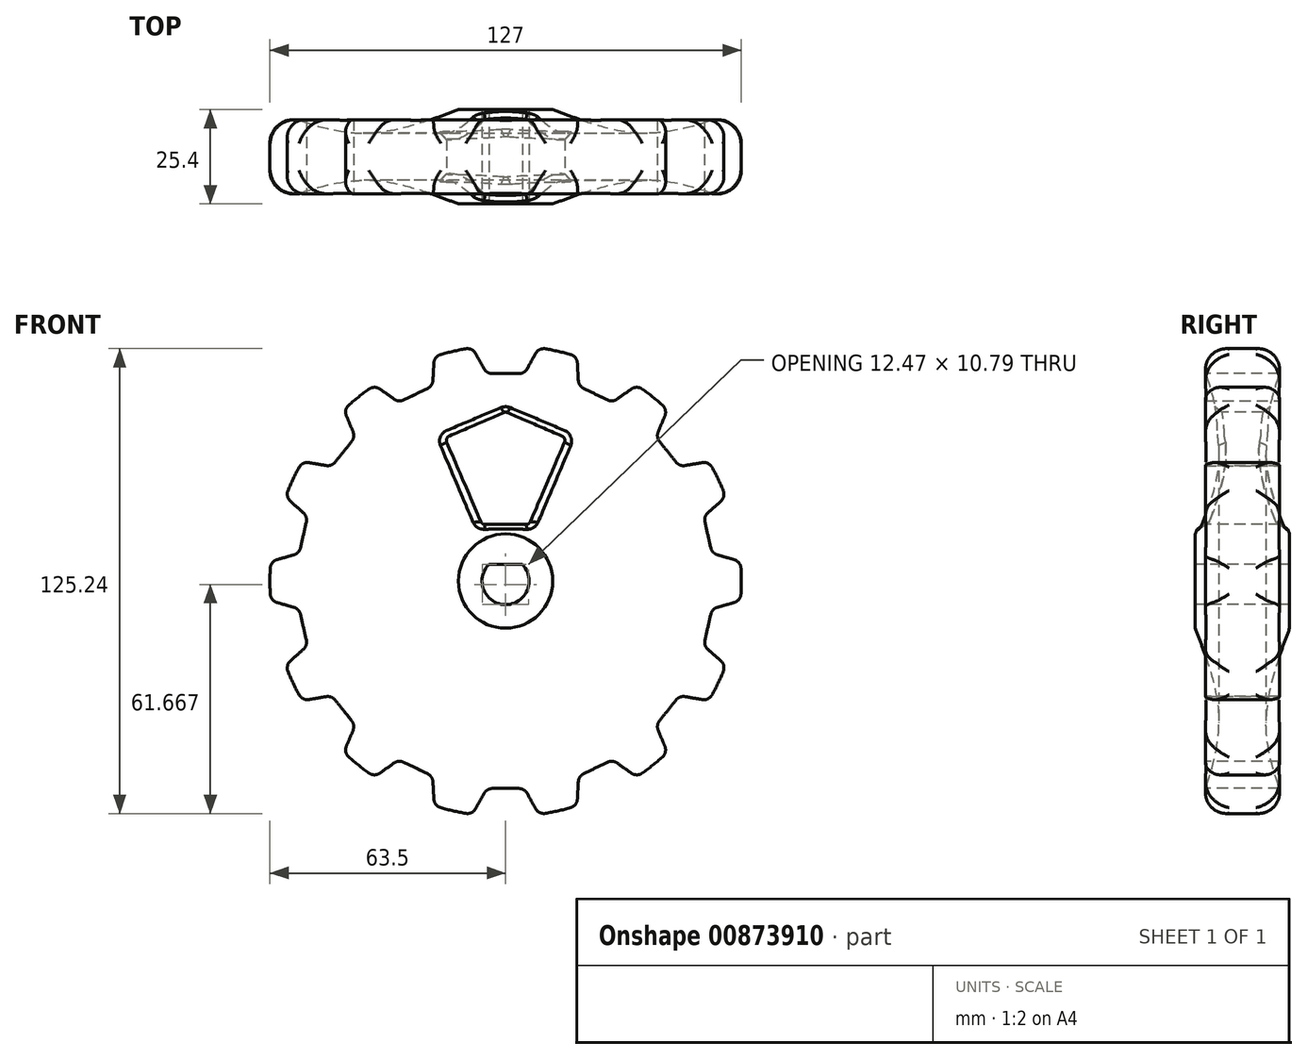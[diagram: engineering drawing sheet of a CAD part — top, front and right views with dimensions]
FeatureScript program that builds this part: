
annotation { "Feature Type Name" : "Feature", "Feature Type Description" : "" }
export const myFeature = defineFeature(function(context is Context, id is Id, definition is map)
    precondition{}
    {
        {
            var Q0;
            Q0=qCreatedBy(makeId("Right.planeOp"),FACE);
            var sketch = newSketch(context, id + "F0", { "sketchPlane" : qUnion([Q0])});
            skLineSegment(sketch, "E0", {"start": v(0, 0) * mm, "end": v(12.7, 0) * mm});
            skLineSegment(sketch, "E1", {"start": v(12.7, 0) * mm, "end": v(12.7, 12.7) * mm});
            skFitSpline(sketch, "E2", {"points": [v(12.7, 63.5) * mm, v(6.35, 38.1) * mm, v(12.7, 12.7) * mm], "startDerivative": vector(-19.05, -50.8) * mm, "endDerivative": vector(19.05, -50.8) * mm});
            skLineSegment(sketch, "E3", {"start": v(3.65, 63.5) * mm, "end": v(-3.65, 63.5) * mm});
            skFitSpline(sketch, "E4.MirrorCS", {"points": [v(-12.7, 63.5) * mm, v(-6.35, 38.1) * mm, v(-12.7, 12.7) * mm], "startDerivative": vector(19.05, -50.8) * mm, "endDerivative": vector(-19.05, -50.8) * mm});
            skLineSegment(sketch, "E5.MirrorCS", {"start": v(-12.7, 0) * mm, "end": v(-12.7, 12.7) * mm});
            skLineSegment(sketch, "E6.MirrorCS", {"start": v(0, 0) * mm, "end": v(-12.7, 0) * mm});
            skArc(sketch, "E7.filletArc", {"start": v(9.68, 55.14) * mm, "mid": v(8.8, 60.86) * mm, "end": v(3.65, 63.5) * mm});
            skArc(sketch, "E8.filletArc", {"start": v(-3.65, 63.5) * mm, "mid": v(-8.8, 60.86) * mm, "end": v(-9.68, 55.14) * mm});
            skSolve(sketch);
        }
        {
            var Q0;
            Q0=makeQuery(id+"F0.imprint","IMPRINT",FACE,{"disambiguationData":[TD([[makeQuery(id+"F0.imprint","IMPRINT",EDGE,{"derivedFrom":sQuery(id+"F0.wireOp",EDGE,"E0")}),1.0]])]});
            var Q1;
            Q1=sQuery(id+"F0.wireOp",EDGE,"E6.MirrorCS");
            revolve(context, id + "F1", {"surfaceOperationType" : NewSurfaceOperationType.NEW, "entities" : qUnion([Q0]), "axis" : qUnion([Q1]), "revolveType" : RevolveType.FULL});
        }
        {
            var Q0;
            Q0=qCreatedBy(makeId("Front.planeOp"),FACE);
            var sketch = newSketch(context, id + "F2", { "sketchPlane" : qUnion([Q0])});
            skLineSegment(sketch, "E9", {"start": v(0, 0) * mm, "end": v(0, 55.88) * mm});
            skLineSegment(sketch, "E10", {"start": v(0, 55.88) * mm, "end": v(-5.08, 55.88) * mm});
            skLineSegment(sketch, "E11", {"start": v(0, 55.88) * mm, "end": v(0, 66.04) * mm});
            skLineSegment(sketch, "E12", {"start": v(0, 66.04) * mm, "end": v(-10.67, 66.04) * mm});
            skLineSegment(sketch, "E13", {"start": v(-10.67, 66.04) * mm, "end": v(-5.08, 55.88) * mm});
            skLineSegment(sketch, "E14.MirrorCS", {"start": v(10.67, 66.04) * mm, "end": v(5.08, 55.88) * mm});
            skLineSegment(sketch, "E15.MirrorCS", {"start": v(0, 55.88) * mm, "end": v(5.08, 55.88) * mm});
            skLineSegment(sketch, "E16.MirrorCS", {"start": v(0, 66.04) * mm, "end": v(10.67, 66.04) * mm});
            skSolve(sketch);
        }
        {
            var Q0;
            Q0=makeQuery(id+"F2.imprint","IMPRINT",FACE,{"disambiguationData":[TD([[makeQuery(id+"F2.imprint","IMPRINT",EDGE,{"derivedFrom":sQuery(id+"F2.wireOp",EDGE,"E11")}),-1.0]])]});
            var Q1;
            Q1=makeQuery(id+"F2.imprint","IMPRINT",FACE,{"disambiguationData":[TD([[makeQuery(id+"F2.imprint","IMPRINT",EDGE,{"derivedFrom":sQuery(id+"F2.wireOp",EDGE,"E10")}),-1.0]])]});
            extrude(context, id + "F3", {"entities" : qUnion([Q0, Q1]), "operationType" : NewBodyOperationType.REMOVE, "oppositeDirection" : true, "depth" : 25.4 * mm, "offsetDistance" : 25.4 * mm, "symmetric" : true});
        }
        {
            var Q0;
            Q0=makeQuery(id+"F3.boolean.opBoolean","COPY",EDGE,{"derivedFrom":makeQuery(id+"F3.opExtrude","SWEPT_EDGE",EDGE,{"disambiguationData":[OSD([sQuery(id+"F2.wireOp",EDGE,"E10"),sQuery(id+"F2.wireOp",EDGE,"E13")])]})});
            var Q1;
            Q1=makeQuery(id+"F3.boolean.opBoolean","COPY",EDGE,{"derivedFrom":makeQuery(id+"F3.opExtrude","SWEPT_EDGE",EDGE,{"disambiguationData":[OSD([sQuery(id+"F2.wireOp",EDGE,"E14.MirrorCS"),sQuery(id+"F2.wireOp",EDGE,"E15.MirrorCS")])]})});
            fillet(context, id + "F4", {"entities" : qUnion([Q0, Q1]), "radius" : 2.54 * mm, "tangentPropagation" : true, "allowEdgeOverflow" : false});
        }
        {
            var Q0;
            Q0=makeQuery(id+"F3.boolean.opBoolean","INTERSECT",EDGE,{"derivedFrom":[makeQuery(id+"F1.opRevolve","SWEPT_FACE",FACE,{"disambiguationData":[OSD([sQuery(id+"F0.wireOp",EDGE,"E3")])]}),makeQuery(id+"F3.opExtrude","SWEPT_FACE",FACE,{"disambiguationData":[OSD([sQuery(id+"F2.wireOp",EDGE,"E13")])]})]});
            var Q1;
            Q1=makeQuery(id+"F3.boolean.opBoolean","INTERSECT",EDGE,{"derivedFrom":[makeQuery(id+"F1.opRevolve","SWEPT_FACE",FACE,{"disambiguationData":[OSD([sQuery(id+"F0.wireOp",EDGE,"E3")])]}),makeQuery(id+"F3.opExtrude","SWEPT_FACE",FACE,{"disambiguationData":[OSD([sQuery(id+"F2.wireOp",EDGE,"E14.MirrorCS")])]})]});
            fillet(context, id + "F5", {"entities" : qUnion([Q0, Q1]), "radius" : 2.54 * mm, "allowEdgeOverflow" : false});
        }
        {
            var Q0;
            Q0=makeQuery(id+"F5.opFillet","BLEND_FACE",FACE,{"disambiguationData":[OSD([sQuery(id+"F0.wireOp",EDGE,"E3"),sQuery(id+"F2.wireOp",EDGE,"E14.MirrorCS")])]});
            var Q1;
            Q1=makeQuery(id+"F3.boolean.opBoolean","COPY",FACE,{"derivedFrom":makeQuery(id+"F3.opExtrude","SWEPT_FACE",FACE,{"disambiguationData":[OSD([sQuery(id+"F2.wireOp",EDGE,"E14.MirrorCS")])]})});
            var Q2;
            Q2=makeQuery(id+"F4.opFillet","BLEND_FACE",FACE,{"disambiguationData":[OSD([sQuery(id+"F2.wireOp",EDGE,"E14.MirrorCS"),sQuery(id+"F2.wireOp",EDGE,"E15.MirrorCS")])]});
            var Q3;
            Q3=makeQuery(id+"F3.boolean.opBoolean","COPY",FACE,{"derivedFrom":makeQuery(id+"F3.opExtrude","SWEPT_FACE",FACE,{"disambiguationData":[OSD([sQuery(id+"F2.wireOp",EDGE,"E10"),sQuery(id+"F2.wireOp",EDGE,"E15.MirrorCS")])]})});
            var Q4;
            Q4=makeQuery(id+"F4.opFillet","BLEND_FACE",FACE,{"disambiguationData":[OSD([sQuery(id+"F2.wireOp",EDGE,"E10"),sQuery(id+"F2.wireOp",EDGE,"E13")])]});
            var Q5;
            Q5=makeQuery(id+"F3.boolean.opBoolean","COPY",FACE,{"derivedFrom":makeQuery(id+"F3.opExtrude","SWEPT_FACE",FACE,{"disambiguationData":[OSD([sQuery(id+"F2.wireOp",EDGE,"E13")])]})});
            var Q6;
            Q6=makeQuery(id+"F5.opFillet","BLEND_FACE",FACE,{"disambiguationData":[OSD([sQuery(id+"F0.wireOp",EDGE,"E3"),sQuery(id+"F2.wireOp",EDGE,"E13")])]});
            var Q7;
            Q7=makeQuery(id+"F1.opRevolve","SWEPT_EDGE",EDGE,{"disambiguationData":[OSD([sQuery(id+"F0.wireOp",EDGE,"E4.MirrorCS"),sQuery(id+"F0.wireOp",EDGE,"E5.MirrorCS")])]});
            circularPattern(context, id + "F6", {"patternType" : PatternType.FACE, "faces" : qUnion([Q0, Q1, Q2, Q3, Q4, Q5, Q6]), "axis" : qUnion([Q7]), "angle" : 360 * degree, "instanceCount" : 14, "equalSpace" : true});
        }
        {
            var Q0;
            Q0=makeQuery(id+"F1.opRevolve","SWEPT_FACE",FACE,{"disambiguationData":[OSD([sQuery(id+"F0.wireOp",EDGE,"E5.MirrorCS")])]});
            var sketch = newSketch(context, id + "F7", { "sketchPlane" : qUnion([Q0])});
            skLineSegment(sketch, "E17", {"start": v(0, 0) * mm, "end": v(0, 15.24) * mm});
            skLineSegment(sketch, "E18", {"start": v(0, 15.24) * mm, "end": v(5.51, 15.24) * mm});
            skLineSegment(sketch, "E19", {"start": v(6.68, 16) * mm, "end": v(15.86, 37.42) * mm});
            skLineSegment(sketch, "E20", {"start": v(15.2, 39.08) * mm, "end": v(0.5, 45.39) * mm});
            skPoint(sketch, "E21.visualSharp", {"position": v(16.36, 38.58) * mm});
            skArc(sketch, "E21.filletArc", {"start": v(15.86, 37.42) * mm, "mid": v(15.87, 38.39) * mm, "end": v(15.2, 39.08) * mm});
            skPoint(sketch, "E22.visualSharp", {"position": v(6.35, 15.24) * mm});
            skArc(sketch, "E22.filletArc", {"start": v(5.51, 15.24) * mm, "mid": v(6.21, 15.45) * mm, "end": v(6.68, 16) * mm});
            skLineSegment(sketch, "E23.MirrorCS", {"start": v(-15.2, 39.08) * mm, "end": v(-0.5, 45.39) * mm});
            skArc(sketch, "E24.MirrorCS", {"start": v(-15.86, 37.42) * mm, "mid": v(-15.87, 38.39) * mm, "end": v(-15.2, 39.08) * mm});
            skLineSegment(sketch, "E25.MirrorCS", {"start": v(-6.68, 16) * mm, "end": v(-15.86, 37.42) * mm});
            skArc(sketch, "E26.MirrorCS", {"start": v(-5.51, 15.24) * mm, "mid": v(-6.21, 15.45) * mm, "end": v(-6.68, 16) * mm});
            skLineSegment(sketch, "E27.MirrorCS", {"start": v(0, 15.24) * mm, "end": v(-5.51, 15.24) * mm});
            skPoint(sketch, "E28.visualSharp", {"position": v(0, 45.6) * mm});
            skArc(sketch, "E28.filletArc", {"start": v(0.5, 45.39) * mm, "mid": v(0, 45.49) * mm, "end": v(-0.5, 45.39) * mm});
            skSolve(sketch);
        }
        {
            var Q0;
            Q0=makeQuery(id+"F7.imprint","IMPRINT",FACE,{"disambiguationData":[TD([[makeQuery(id+"F7.imprint","IMPRINT",EDGE,{"derivedFrom":sQuery(id+"F7.wireOp",EDGE,"E18")}),1.0]])]});
            extrude(context, id + "F8", {"entities" : qUnion([Q0]), "operationType" : NewBodyOperationType.REMOVE, "oppositeDirection" : true, "depth" : 25.4 * mm, "offsetDistance" : 25.4 * mm});
        }
        {
            var Q0;
            Q0=makeQuery(id+"F8.boolean.opBoolean","INTERSECT",EDGE,{"derivedFrom":[makeQuery(id+"F1.opRevolve","SWEPT_FACE",FACE,{"disambiguationData":[OSD([sQuery(id+"F0.wireOp",EDGE,"E4.MirrorCS")])]}),makeQuery(id+"F8.opExtrude","SWEPT_FACE",FACE,{"disambiguationData":[OSD([sQuery(id+"F7.wireOp",EDGE,"E23.MirrorCS")])]})]});
            var Q1;
            Q1=makeQuery(id+"FnRsK331Qt2ESd3_1.4.F8.boolean.opBoolean","INTERSECT",EDGE,{"derivedFrom":[makeQuery(id+"F1.opRevolve","SWEPT_FACE",FACE,{"disambiguationData":[OSD([sQuery(id+"F0.wireOp",EDGE,"E4.MirrorCS")])]}),makeQuery(id+"FnRsK331Qt2ESd3_1.4.F8.opExtrude","SWEPT_FACE",FACE,{"disambiguationData":[OSD([sQuery(id+"F7.wireOp",EDGE,"E19")])]})]});
            var Q2;
            Q2=makeQuery(id+"FnRsK331Qt2ESd3_1.1.F8.boolean.opBoolean","INTERSECT",EDGE,{"derivedFrom":[makeQuery(id+"F1.opRevolve","SWEPT_FACE",FACE,{"disambiguationData":[OSD([sQuery(id+"F0.wireOp",EDGE,"E4.MirrorCS")])]}),makeQuery(id+"FnRsK331Qt2ESd3_1.1.F8.opExtrude","SWEPT_FACE",FACE,{"disambiguationData":[OSD([sQuery(id+"F7.wireOp",EDGE,"E25.MirrorCS")])]})]});
            var Q3;
            Q3=makeQuery(id+"FnRsK331Qt2ESd3_1.2.F8.boolean.opBoolean","INTERSECT",EDGE,{"derivedFrom":[makeQuery(id+"F1.opRevolve","SWEPT_FACE",FACE,{"disambiguationData":[OSD([sQuery(id+"F0.wireOp",EDGE,"E4.MirrorCS")])]}),makeQuery(id+"FnRsK331Qt2ESd3_1.2.F8.opExtrude","SWEPT_FACE",FACE,{"disambiguationData":[OSD([sQuery(id+"F7.wireOp",EDGE,"E25.MirrorCS")])]})]});
            var Q4;
            Q4=makeQuery(id+"FnRsK331Qt2ESd3_1.3.F8.boolean.opBoolean","INTERSECT",EDGE,{"derivedFrom":[makeQuery(id+"F1.opRevolve","SWEPT_FACE",FACE,{"disambiguationData":[OSD([sQuery(id+"F0.wireOp",EDGE,"E4.MirrorCS")])]}),makeQuery(id+"FnRsK331Qt2ESd3_1.3.F8.opExtrude","SWEPT_FACE",FACE,{"disambiguationData":[OSD([sQuery(id+"F7.wireOp",EDGE,"E25.MirrorCS")])]})]});
            var Q5;
            Q5=makeQuery(id+"F8.boolean.opBoolean","INTERSECT",EDGE,{"derivedFrom":[makeQuery(id+"F1.opRevolve","SWEPT_FACE",FACE,{"disambiguationData":[OSD([sQuery(id+"F0.wireOp",EDGE,"E2")])]}),makeQuery(id+"F8.opExtrude","SWEPT_FACE",FACE,{"disambiguationData":[OSD([sQuery(id+"F7.wireOp",EDGE,"E25.MirrorCS")])]})]});
            var Q6;
            Q6=makeQuery(id+"FnRsK331Qt2ESd3_1.1.F8.boolean.opBoolean","INTERSECT",EDGE,{"derivedFrom":[makeQuery(id+"F1.opRevolve","SWEPT_FACE",FACE,{"disambiguationData":[OSD([sQuery(id+"F0.wireOp",EDGE,"E2")])]}),makeQuery(id+"FnRsK331Qt2ESd3_1.1.F8.opExtrude","SWEPT_FACE",FACE,{"disambiguationData":[OSD([sQuery(id+"F7.wireOp",EDGE,"E25.MirrorCS")])]})]});
            var Q7;
            Q7=makeQuery(id+"FnRsK331Qt2ESd3_1.2.F8.boolean.opBoolean","INTERSECT",EDGE,{"derivedFrom":[makeQuery(id+"F1.opRevolve","SWEPT_FACE",FACE,{"disambiguationData":[OSD([sQuery(id+"F0.wireOp",EDGE,"E2")])]}),makeQuery(id+"FnRsK331Qt2ESd3_1.2.F8.opExtrude","SWEPT_FACE",FACE,{"disambiguationData":[OSD([sQuery(id+"F7.wireOp",EDGE,"E25.MirrorCS")])]})]});
            var Q8;
            Q8=makeQuery(id+"FnRsK331Qt2ESd3_1.2.F8.boolean.opBoolean","INTERSECT",EDGE,{"derivedFrom":[makeQuery(id+"F1.opRevolve","SWEPT_FACE",FACE,{"disambiguationData":[OSD([sQuery(id+"F0.wireOp",EDGE,"E2")])]}),makeQuery(id+"FnRsK331Qt2ESd3_1.2.F8.opExtrude","SWEPT_FACE",FACE,{"disambiguationData":[OSD([sQuery(id+"F7.wireOp",EDGE,"E19")])]})]});
            var Q9;
            Q9=makeQuery(id+"FnRsK331Qt2ESd3_1.3.F8.boolean.opBoolean","INTERSECT",EDGE,{"derivedFrom":[makeQuery(id+"F1.opRevolve","SWEPT_FACE",FACE,{"disambiguationData":[OSD([sQuery(id+"F0.wireOp",EDGE,"E2")])]}),makeQuery(id+"FnRsK331Qt2ESd3_1.3.F8.opExtrude","SWEPT_FACE",FACE,{"disambiguationData":[OSD([sQuery(id+"F7.wireOp",EDGE,"E19")])]})]});
            var Q10;
            Q10=makeQuery(id+"FnRsK331Qt2ESd3_1.4.F8.boolean.opBoolean","INTERSECT",EDGE,{"derivedFrom":[makeQuery(id+"F1.opRevolve","SWEPT_FACE",FACE,{"disambiguationData":[OSD([sQuery(id+"F0.wireOp",EDGE,"E2")])]}),makeQuery(id+"FnRsK331Qt2ESd3_1.4.F8.opExtrude","SWEPT_FACE",FACE,{"disambiguationData":[OSD([sQuery(id+"F7.wireOp",EDGE,"E19")])]})]});
            chamfer(context, id + "F9", {"entities" : qUnion([Q0, Q1, Q2, Q3, Q4, Q5, Q6, Q7, Q8, Q9, Q10]), "width" : 1.9 * mm, "tangentPropagation" : true});
        }
        {
            var Q0;
            Q0=makeQuery(id+"F1.opRevolve","SWEPT_FACE",FACE,{"disambiguationData":[OSD([sQuery(id+"F0.wireOp",EDGE,"E5.MirrorCS")])]});
            var sketch = newSketch(context, id + "F10", { "sketchPlane" : qUnion([Q0])});
            skCircle(sketch, "E29", {"center": v(0, 0) * mm, "radius": 6.35 * mm});
            skLineSegment(sketch, "E30", {"start": v(0, 0) * mm, "end": v(0, 4.45) * mm});
            skLineSegment(sketch, "E31", {"start": v(0, 4.45) * mm, "end": v(4.53, 4.45) * mm});
            skLineSegment(sketch, "E32", {"start": v(0, 4.45) * mm, "end": v(-4.53, 4.45) * mm});
            skSolve(sketch);
        }
        {
            var Q0;
            {var subQ0=sQuery(id+"F10.wireOp",EDGE,"E31");Q0=makeQuery(id+"F10.imprint","IMPRINT",FACE,{"disambiguationData":[TD([[makeQuery(id+"F10.imprint","IMPRINT",EDGE,{"derivedFrom":subQ0}),-1.0]])]});}
            extrude(context, id + "F11", {"entities" : qUnion([Q0]), "operationType" : NewBodyOperationType.REMOVE, "oppositeDirection" : true, "depth" : 30.23 * mm, "offsetDistance" : 25.4 * mm});
        }
    });
